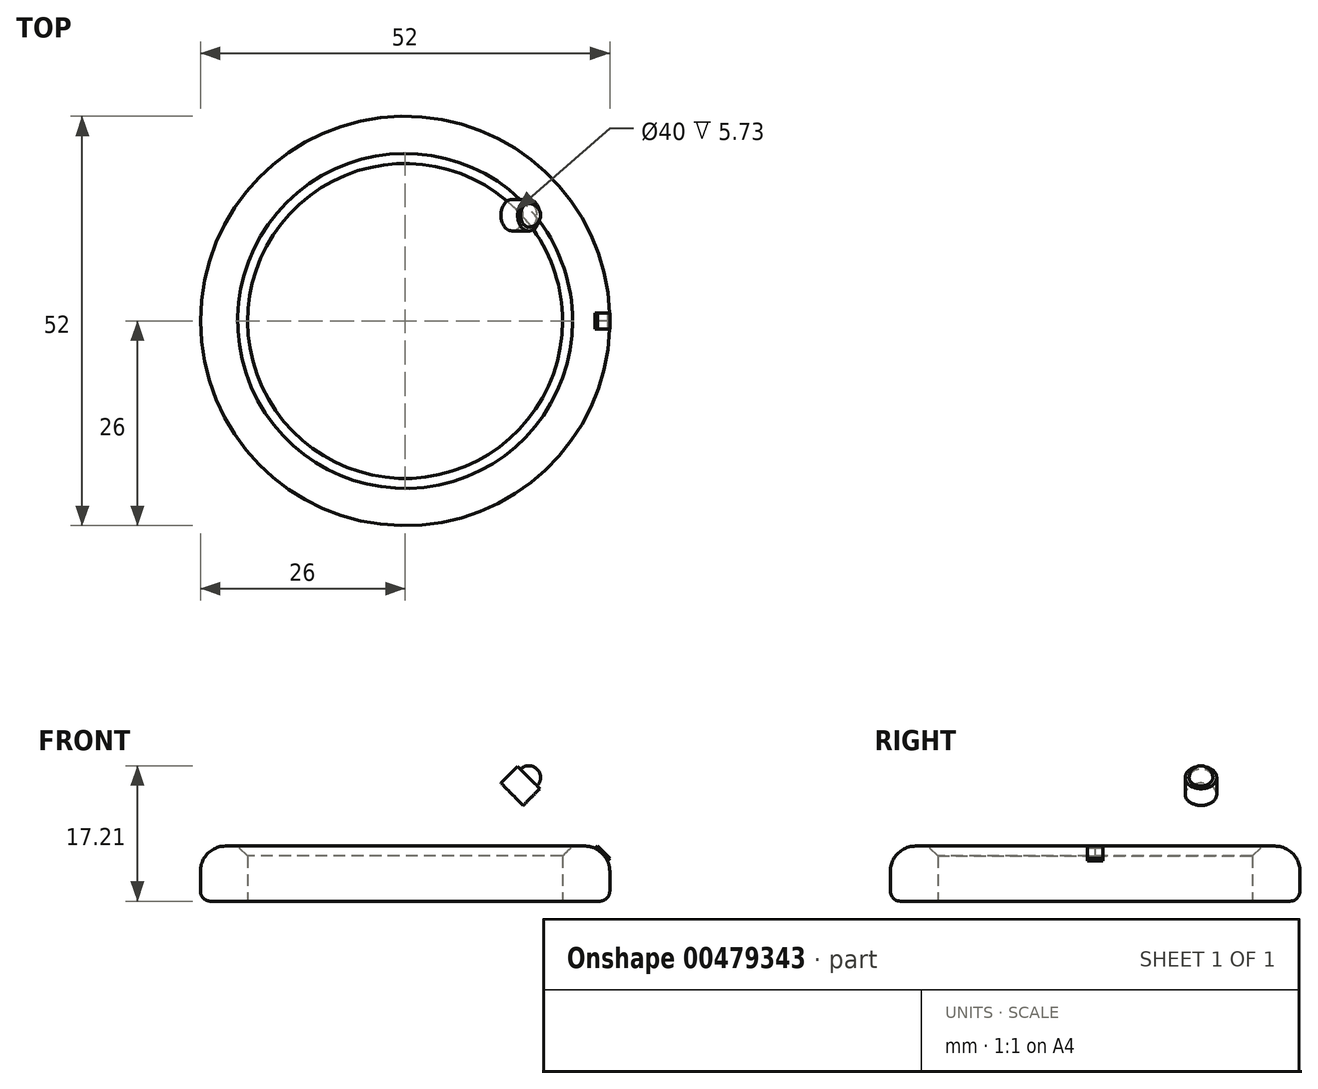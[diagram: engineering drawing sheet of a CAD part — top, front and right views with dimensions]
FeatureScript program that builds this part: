
annotation { "Feature Type Name" : "Feature", "Feature Type Description" : "" }
export const myFeature = defineFeature(function(context is Context, id is Id, definition is map)
    precondition{}
    {
        {
            var Q0;
            Q0=qCreatedBy(makeId("Top.planeOp"),FACE);
            var sketch = newSketch(context, id + "F0", { "sketchPlane" : qUnion([Q0])});
            skCircle(sketch, "E0", {"center": v(0, 0) * mm, "radius": 26 * mm});
            skCircle(sketch, "E1", {"center": v(0, 0) * mm, "radius": 20 * mm});
            skSolve(sketch);
        }
        {
            var Q0;
            Q0=makeQuery(id+"F0.imprint","IMPRINT",FACE,{"disambiguationData":[TD([[makeQuery(id+"F0.imprint","IMPRINT",EDGE,{"derivedFrom":sQuery(id+"F0.wireOp",EDGE,"E0")}),1.0]])]});
            extrude(context, id + "F1", {"entities" : qUnion([Q0]), "depth" : 7 * mm, "offsetDistance" : 25.4 * mm});
        }
        {
            var Q0;
            Q0=makeQuery(id+"F1.opExtrude","CAP_EDGE",EDGE,{"disambiguationData":[OSD([sQuery(id+"F0.wireOp",EDGE,"E0")])],"isStart":false});
            fillet(context, id + "F2", {"entities" : qUnion([Q0]), "radius" : 3.17 * mm, "tangentPropagation" : true, "allowEdgeOverflow" : false});
        }
        {
            var Q0;
            Q0=makeQuery(id+"F1.opExtrude","CAP_EDGE",EDGE,{"disambiguationData":[OSD([sQuery(id+"F0.wireOp",EDGE,"E1")])],"isStart":false});
            chamfer(context, id + "F3", {"entities" : qUnion([Q0]), "width" : 1.27 * mm, "tangentPropagation" : true});
        }
        {
            var Q0;
            Q0=makeQuery(id+"F1.opExtrude","CAP_EDGE",EDGE,{"disambiguationData":[OSD([sQuery(id+"F0.wireOp",EDGE,"E0")])],"isStart":true});
            fillet(context, id + "F4", {"entities" : qUnion([Q0]), "radius" : 1.27 * mm, "tangentPropagation" : true, "allowEdgeOverflow" : false});
        }
        {
            var Q0;
            Q0=qCreatedBy(makeId("Front.planeOp"),FACE);
            var sketch = newSketch(context, id + "F5", { "sketchPlane" : qUnion([Q0])});
            skLineSegment(sketch, "E2", {"start": v(0, 0) * mm, "end": v(26, 0) * mm, "construction": true});
            skLineSegment(sketch, "E3", {"start": v(0, 0) * mm, "end": v(0, 7) * mm, "construction": true});
            skLineSegment(sketch, "E4.bottom", {"start": v(0, 0) * mm, "end": v(26, 0) * mm});
            skLineSegment(sketch, "E4.top", {"start": v(0, 7) * mm, "end": v(26, 7) * mm});
            skLineSegment(sketch, "E4.left", {"start": v(0, 0) * mm, "end": v(0, 7) * mm});
            skLineSegment(sketch, "E4.right", {"start": v(26, 0) * mm, "end": v(26, 7) * mm});
            skLineSegment(sketch, "E5", {"start": v(26, 7) * mm, "end": v(26, 3.83) * mm});
            skLineSegment(sketch, "E6", {"start": v(26, 7) * mm, "end": v(22.83, 7) * mm});
            skLineSegment(sketch, "E7", {"start": v(22.83, 7) * mm, "end": v(26, 3.83) * mm});
            skLineSegment(sketch, "E8", {"start": v(25.2, 6.2) * mm, "end": v(26, 7) * mm});
            skLineSegment(sketch, "E9", {"start": v(24.41, 5.41) * mm, "end": v(26, 3.83) * mm});
            skLineSegment(sketch, "E10", {"start": v(25.2, 4.62) * mm, "end": v(26, 5.41) * mm});
            skLineSegment(sketch, "E11", {"start": v(24.41, 5.41) * mm, "end": v(22.83, 7) * mm});
            skLineSegment(sketch, "E12", {"start": v(23.62, 6.2) * mm, "end": v(24.41, 7) * mm});
            skLineSegment(sketch, "E13", {"start": v(24.41, 7) * mm, "end": v(26, 5.41) * mm});
            skSolve(sketch);
        }
        {
            var Q0;
            {var subQ4=sQuery(id+"F5.wireOp",EDGE,"E10");Q0=makeQuery(id+"F5.imprint","IMPRINT",FACE,{"disambiguationData":[TD([[makeQuery(id+"F5.imprint","IMPRINT",EDGE,{"derivedFrom":subQ4}),1.0]])]});}
            extrude(context, id + "F6", {"entities" : qUnion([Q0]), "operationType" : NewBodyOperationType.ADD, "depth" : 1 * mm, "offsetDistance" : 25.4 * mm});
        }
        {
            var Q0;
            Q0=makeQuery(id+"F6.opExtrude","CAP_FACE",FACE,{"disambiguationData":[OSD([sQuery(id+"F5.wireOp",EDGE,"E9"),sQuery(id+"F5.wireOp",EDGE,"E10"),sQuery(id+"F5.wireOp",EDGE,"E11"),sQuery(id+"F5.wireOp",EDGE,"E12"),sQuery(id+"F5.wireOp",EDGE,"E13")])],"isStart":true});
            extrude(context, id + "F7", {"entities" : qUnion([Q0]), "operationType" : NewBodyOperationType.ADD, "depth" : 1 * mm, "offsetDistance" : 25.4 * mm});
        }
        {
            var Q0;
            {var subQ0=sQuery(id+"F5.wireOp",EDGE,"E13");Q0=makeQuery(id+"F7.boolean.opBoolean","MERGE",FACE,{"derivedFrom":[makeQuery(id+"F6.opExtrude","SWEPT_FACE",FACE,{"disambiguationData":[OSD([subQ0])]}),makeQuery(id+"F7.opExtrude","SWEPT_FACE",FACE,{"disambiguationData":[OSD([subQ0])]})]});}
            var sketch = newSketch(context, id + "F8", { "sketchPlane" : qUnion([Q0])});
            skLineSegment(sketch, "E14", {"start": v(12.31, 0) * mm, "end": v(14.56, 0) * mm, "construction": true});
            skCircle(sketch, "E15", {"center": v(13.44, 0) * mm, "radius": 2 * mm});
            skSolve(sketch);
        }
        {
            var Q0;
            Q0=makeQuery(id+"F8.imprint","IMPRINT",FACE,{"disambiguationData":[TD([[makeQuery(id+"F8.imprint","IMPRINT",EDGE,{"derivedFrom":sQuery(id+"F8.wireOp",EDGE,"E15")}),1.0]])]});
            extrude(context, id + "F9", {"entities" : qUnion([Q0]), "operationType" : NewBodyOperationType.ADD, "oppositeDirection" : true, "depth" : 3 * mm, "offsetDistance" : 25.4 * mm});
        }
        {
            var Q0;
            {var subQ0=sQuery(id+"F5.wireOp",EDGE,"E13");Q0=makeQuery(id+"F9.boolean.opBoolean","MERGE",FACE,{"derivedFrom":[makeQuery(id+"F7.boolean.opBoolean","MERGE",FACE,{"derivedFrom":[makeQuery(id+"F6.opExtrude","SWEPT_FACE",FACE,{"disambiguationData":[OSD([subQ0])]}),makeQuery(id+"F7.opExtrude","SWEPT_FACE",FACE,{"disambiguationData":[OSD([subQ0])]})]}),makeQuery(id+"F9.opExtrude","CAP_FACE",FACE,{"disambiguationData":[OSD([sQuery(id+"F5.wireOp",EDGE,"E5"),sQuery(id+"F5.wireOp",EDGE,"E6"),sQuery(id+"F5.wireOp",EDGE,"E10"),sQuery(id+"F5.wireOp",EDGE,"E12"),subQ0,sQuery(id+"F8.wireOp",EDGE,"E15")])],"isStart":true})]});}
            var sketch = newSketch(context, id + "F10", { "sketchPlane" : qUnion([Q0])});
            skCircle(sketch, "E16", {"center": v(13.44, 0) * mm, "radius": 1.5 * mm});
            skLineSegment(sketch, "E17", {"start": v(13.44, 0) * mm, "end": v(15.44, 0) * mm});
            skLineSegment(sketch, "E18", {"start": v(13.44, 0) * mm, "end": v(11.44, 0) * mm});
            skSolve(sketch);
        }
        {
            var Q0;
            {var subQ0=sQuery(id+"F10.wireOp",EDGE,"E17");var subQ1=sQuery(id+"F10.wireOp",EDGE,"E16");var subQ2=makeQuery(id+"F10.imprint","INTERSECT",VERTEX,{"derivedFrom":[subQ1,subQ0]});Q0=makeQuery(id+"F10.imprint","IMPRINT",FACE,{"disambiguationData":[TD([[makeQuery(id+"F10.imprint","IMPRINT",EDGE,{"disambiguationData":[TD([[subQ2,-1.0]])],"derivedFrom":subQ1}),1.0]])]});}
            var Q1;
            Q1=sQuery(id+"F10.wireOp",EDGE,"E18");
            revolve(context, id + "F11", {"operationType" : NewBodyOperationType.ADD, "entities" : qUnion([Q0]), "axis" : qUnion([Q1]), "revolveType" : RevolveType.FULL});
        }
    });
